# Revit family: QF_ELECTROLUXPROFESSIONAL_535130_NMPWDRE5M
name_source: partatom
category: Specialty Equipment
revit_build: Autodesk Revit 2018 (Build: 20190510_1515(x64)
units: mm (PartAtom-declared; Revit-internal decimal feet)

## family parameters
Always vertical = Yes
Cut with Voids When Loaded = No
Part Type = Normal
Room Calculation Point = No
Round Connector Dimension = Use Diameter
Shared = No
Work Plane-Based = No

## types (2) — shared parameters
Accessory = Yes
Compressed Air Pressure = 0.0 Pa
Compressed Air Size = 0 mm
Compressed Air Volume = 0.0 L/s
Condensate Return Size = 0 mm
Depth Actual = 825 mm  [stored 2.70669 ft]
Direct Waste Size = 50 mm
Gas Input Pressure = 0
Gas Size = 0 mm
HP = 9.9 HP
Height Actual = 1785 mm  [stored 5.8563 ft]
Length Actual = 560 mm  [stored 1.83727 ft]
Refrigerant Compressor Remote = Yes
Refrigeration Liquid Line Size = 0 mm
Refrigeration Suction Line Size = 0 mm
Steam Supply Maximum Pressure = 0.0 Pa
Steam Supply Minimum Pressure = 0.0 Pa
Steam Supply Size = 0 mm
URL = http://professional.electrolux.com
Watts = 0 W
Weight = 104.00 kg
zero-valued in all types: Gas KW, Steam Pounds per Hour

## per-type parameters (varying)
| type | Cold Water Size | Cycle | Description | Hot Water Size | Item Number | Manufacturer | Model | Phase | URL Manufacturer | Volts |
| NMPWDRE5 | 0 mm | 0 Hz | SINGLE RINSE RT, 100R/H, ELECTRIC 50HZ | 0 mm |  | Electrolux | ESR10E5 | 0 |  | 0 V |
| Standard | 19 mm | 50 Hz | MEDIUM PRE-WASH MODULE, DUAL RINSE RT, ELECTRIC, 400V/ 3/ 50Hz-MARINE | 19 mm | 535130 | Electrolux Professional | NMPWDRE5M | 3 | http://professional.electrolux.com | 400 V |

note: source unit labels omitted for Gas Input Pressure — the stored unit's dimension contradicts the parameter name (converter mislabeling)

note: [stored X ft] marks values corroborated as IEEE doubles in the binary element streams (Revit-internal decimal feet)
